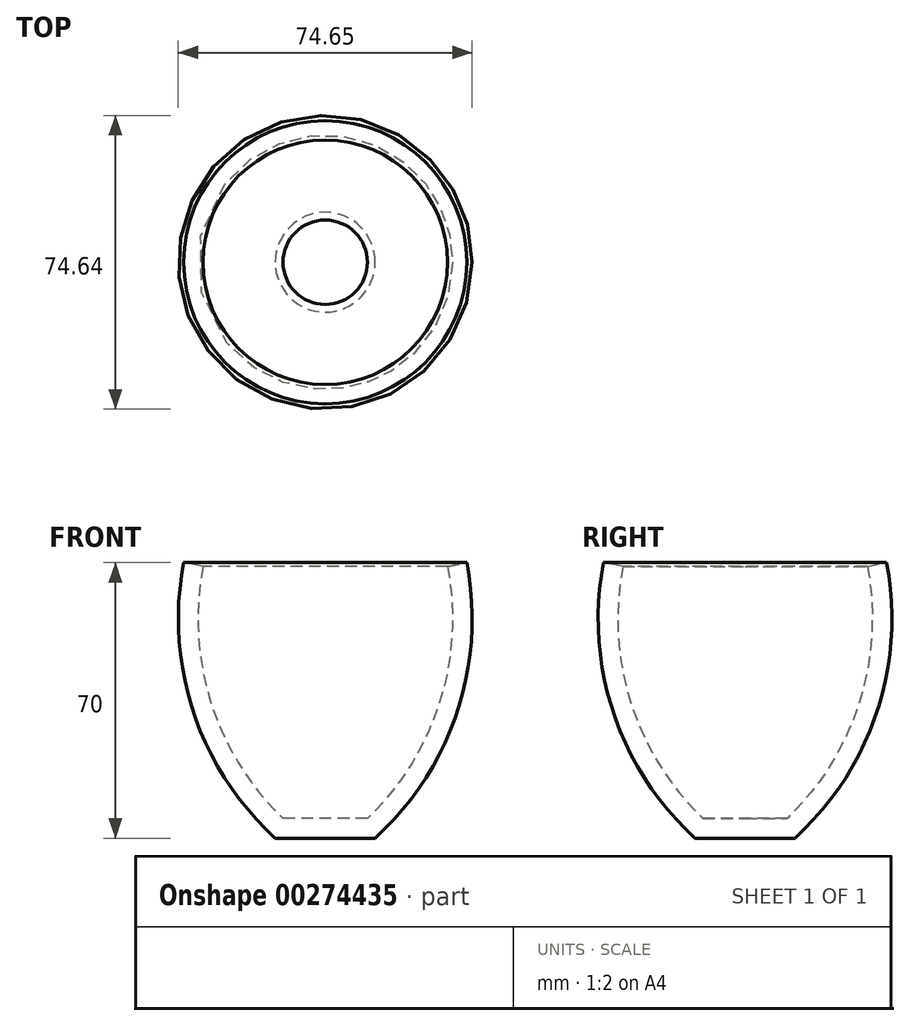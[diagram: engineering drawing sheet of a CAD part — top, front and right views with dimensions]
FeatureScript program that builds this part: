
annotation { "Feature Type Name" : "Feature", "Feature Type Description" : "" }
export const myFeature = defineFeature(function(context is Context, id is Id, definition is map)
    precondition{}
    {
        {
            var Q0;
            Q0=qCreatedBy(makeId("Front.planeOp"),FACE);
            var sketch = newSketch(context, id + "F0", { "sketchPlane" : qUnion([Q0])});
            skLineSegment(sketch, "E0", {"start": v(4.2, 0) * mm, "end": v(14.9, 0) * mm});
            skArc(sketch, "E1", {"start": v(14.9, 0) * mm, "mid": v(33.22, 29.44) * mm, "end": v(35.24, 64.05) * mm});
            skArc(sketch, "E2.0", {"start": v(16.88, -5) * mm, "mid": v(37.67, 26.96) * mm, "end": v(40.15, 65) * mm});
            skLineSegment(sketch, "E2.1", {"start": v(4.2, -5) * mm, "end": v(16.88, -5) * mm});
            skLineSegment(sketch, "E3", {"start": v(4.2, 0) * mm, "end": v(4.2, -5) * mm});
            skLineSegment(sketch, "E4", {"start": v(40.15, 65) * mm, "end": v(35.24, 64.05) * mm});
            skSolve(sketch);
        }
        {
            var Q0;
            Q0=makeQuery(id+"F0.imprint","IMPRINT",FACE,{"disambiguationData":[TD([[makeQuery(id+"F0.imprint","IMPRINT",EDGE,{"derivedFrom":sQuery(id+"F0.wireOp",EDGE,"E0")}),-1.0]])]});
            var Q1;
            Q1=sQuery(id+"F0.wireOp",EDGE,"E3");
            revolve(context, id + "F1", {"entities" : qUnion([Q0]), "axis" : qUnion([Q1]), "revolveType" : RevolveType.FULL});
        }
    });
